# Revit family: revitupgrade
name_source: partatom
category: Furniture
units: mm (PartAtom-declared; Revit-internal decimal feet)

## family parameters
Always vertical = Yes
Cut with Voids When Loaded = No
Enable Cutting in Views = No
OmniClass Number = 23.40.70.14.64.11
OmniClass Title = Office Furniture
Render Appearance Source = Family Geometry
Room Calculation Point = No
Shared = No
Work Plane-Based = No

## types (2) — shared parameters
Arm Cap = Steelcase - 6205 Black
Assembly Code = E2020200
Back Frame = Steelcase - 7207 Black
Default Elevation = 0.00 mm
Description = Choices for seating are abundant with Reply — a complete global family of task and guest chairs that are as nice to look at as they are to sit in.
Glides/Casters = Steelcase - 6205 Black
Manufacturer = Steelcase
Mesh Back = Yes
Release Date = April 2018
URL = https://www.steelcase.com
Upholstery Back = No

## per-type parameters (varying)
| type | Frame | Style Number(s) |
| Platinum Leg | Steelcase - 4799 Platinum Metallic | RPY-82000, RPY-82200 |
| Black Leg | Steelcase - 7207 Black | RPY-72000, RPY-72200 |

## geometry (parser evidence)
native form markers: Sweep x3
no freeform markers — native parametric forms only
